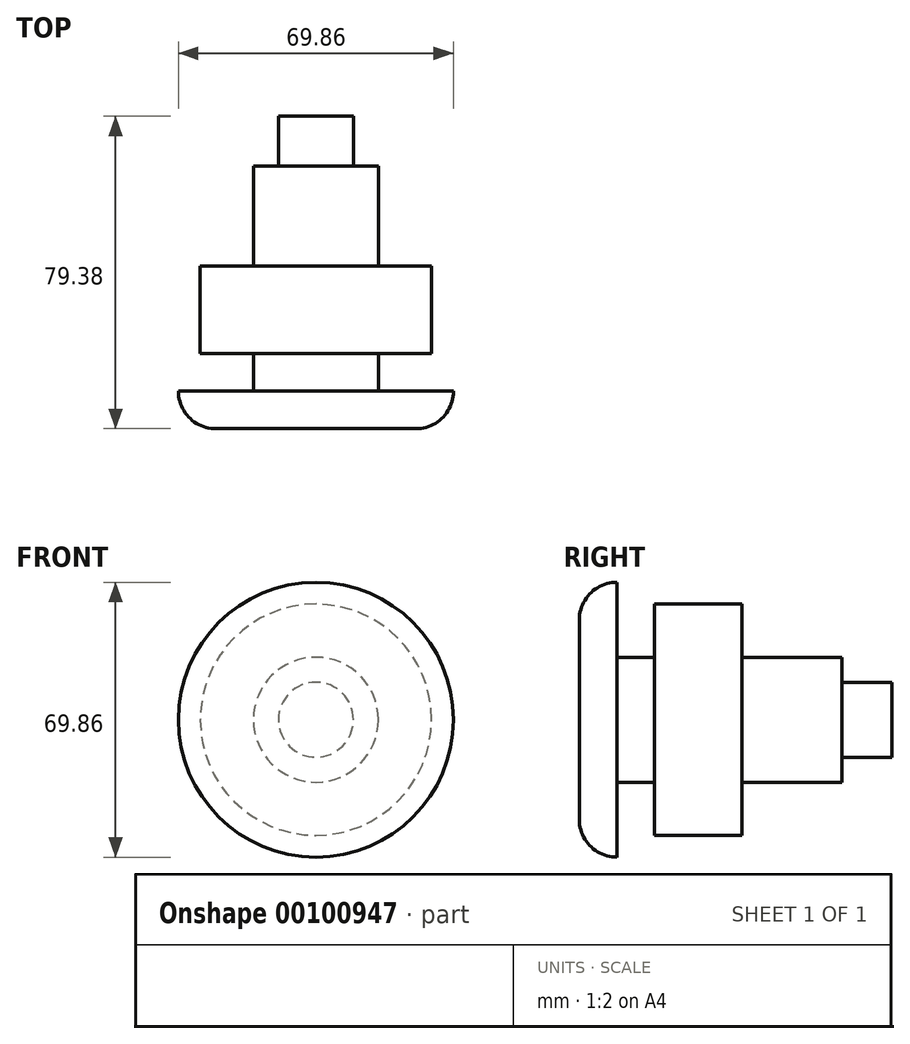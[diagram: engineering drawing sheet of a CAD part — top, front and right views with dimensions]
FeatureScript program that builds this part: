
annotation { "Feature Type Name" : "Feature", "Feature Type Description" : "" }
export const myFeature = defineFeature(function(context is Context, id is Id, definition is map)
    precondition{}
    {
        {
            var Q0;
            Q0=qCreatedBy(makeId("Front.planeOp"),FACE);
            var sketch = newSketch(context, id + "F0", { "sketchPlane" : qUnion([Q0])});
            skCircle(sketch, "E0", {"center": v(0, 0) * mm, "radius": 15.88 * mm});
            skSolve(sketch);
        }
        {
            var Q0;
            Q0 = qSketchRegion(id + "F0", true);
            extrude(context, id + "F1", {"entities" : qUnion([Q0]), "oppositeDirection" : true, "depth" : 9.52 * mm});
        }
        {
            var Q0;
            Q0=makeQuery(id+"F1.opExtrude","CAP_FACE",FACE,{"disambiguationData":[OSD([sQuery(id+"F0.wireOp",EDGE,"E0")])],"isStart":false});
            var sketch = newSketch(context, id + "F2", { "sketchPlane" : qUnion([Q0])});
            skCircle(sketch, "E1", {"center": v(0, 0) * mm, "radius": 29.37 * mm});
            skSolve(sketch);
        }
        {
            var Q0;
            Q0 = qSketchRegion(id + "F2", true);
            extrude(context, id + "F3", {"entities" : qUnion([Q0]), "operationType" : NewBodyOperationType.ADD, "depth" : 22.22 * mm});
        }
        {
            var Q0;
            Q0=makeQuery(id+"F3.opExtrude","CAP_FACE",FACE,{"disambiguationData":[OSD([sQuery(id+"F2.wireOp",EDGE,"E1")])],"isStart":false});
            var sketch = newSketch(context, id + "F4", { "sketchPlane" : qUnion([Q0])});
            skCircle(sketch, "E2", {"center": v(0, 0) * mm, "radius": 15.88 * mm});
            skSolve(sketch);
        }
        {
            var Q0;
            Q0 = qSketchRegion(id + "F4", true);
            extrude(context, id + "F5", {"entities" : qUnion([Q0]), "operationType" : NewBodyOperationType.ADD, "depth" : 25.4 * mm});
        }
        {
            var Q0;
            Q0=makeQuery(id+"F5.opExtrude","CAP_FACE",FACE,{"disambiguationData":[OSD([sQuery(id+"F4.wireOp",EDGE,"E2")])],"isStart":false});
            var sketch = newSketch(context, id + "F6", { "sketchPlane" : qUnion([Q0])});
            skCircle(sketch, "E3", {"center": v(0, 0) * mm, "radius": 9.53 * mm});
            skSolve(sketch);
        }
        {
            var Q0;
            Q0 = qSketchRegion(id + "F6", true);
            extrude(context, id + "F7", {"entities" : qUnion([Q0]), "operationType" : NewBodyOperationType.ADD, "depth" : 12.7 * mm});
        }
        {
            var Q0;
            Q0=makeQuery(id+"F0.imprint","IMPRINT",FACE,{"disambiguationData":[TD([[makeQuery(id+"F0.imprint","IMPRINT",EDGE,{"derivedFrom":sQuery(id+"F0.wireOp",EDGE,"E0")}),1.0]])]});
            var sketch = newSketch(context, id + "F8", { "sketchPlane" : qUnion([Q0])});
            skCircle(sketch, "E4", {"center": v(0, 0) * mm, "radius": 34.93 * mm});
            skSolve(sketch);
        }
        {
            var Q0;
            Q0 = qSketchRegion(id + "F8", true);
            extrude(context, id + "F9", {"entities" : qUnion([Q0]), "operationType" : NewBodyOperationType.ADD, "depth" : 9.52 * mm});
        }
        {
            var Q0;
            Q0=makeQuery(id+"F9.opExtrude","CAP_EDGE",EDGE,{"disambiguationData":[OSD([sQuery(id+"F8.wireOp",EDGE,"E4")])],"isStart":false});
            fillet(context, id + "F10", {"entities" : qUnion([Q0]), "radius" : 9.52 * mm, "tangentPropagation" : true, "allowEdgeOverflow" : false});
        }
    });
